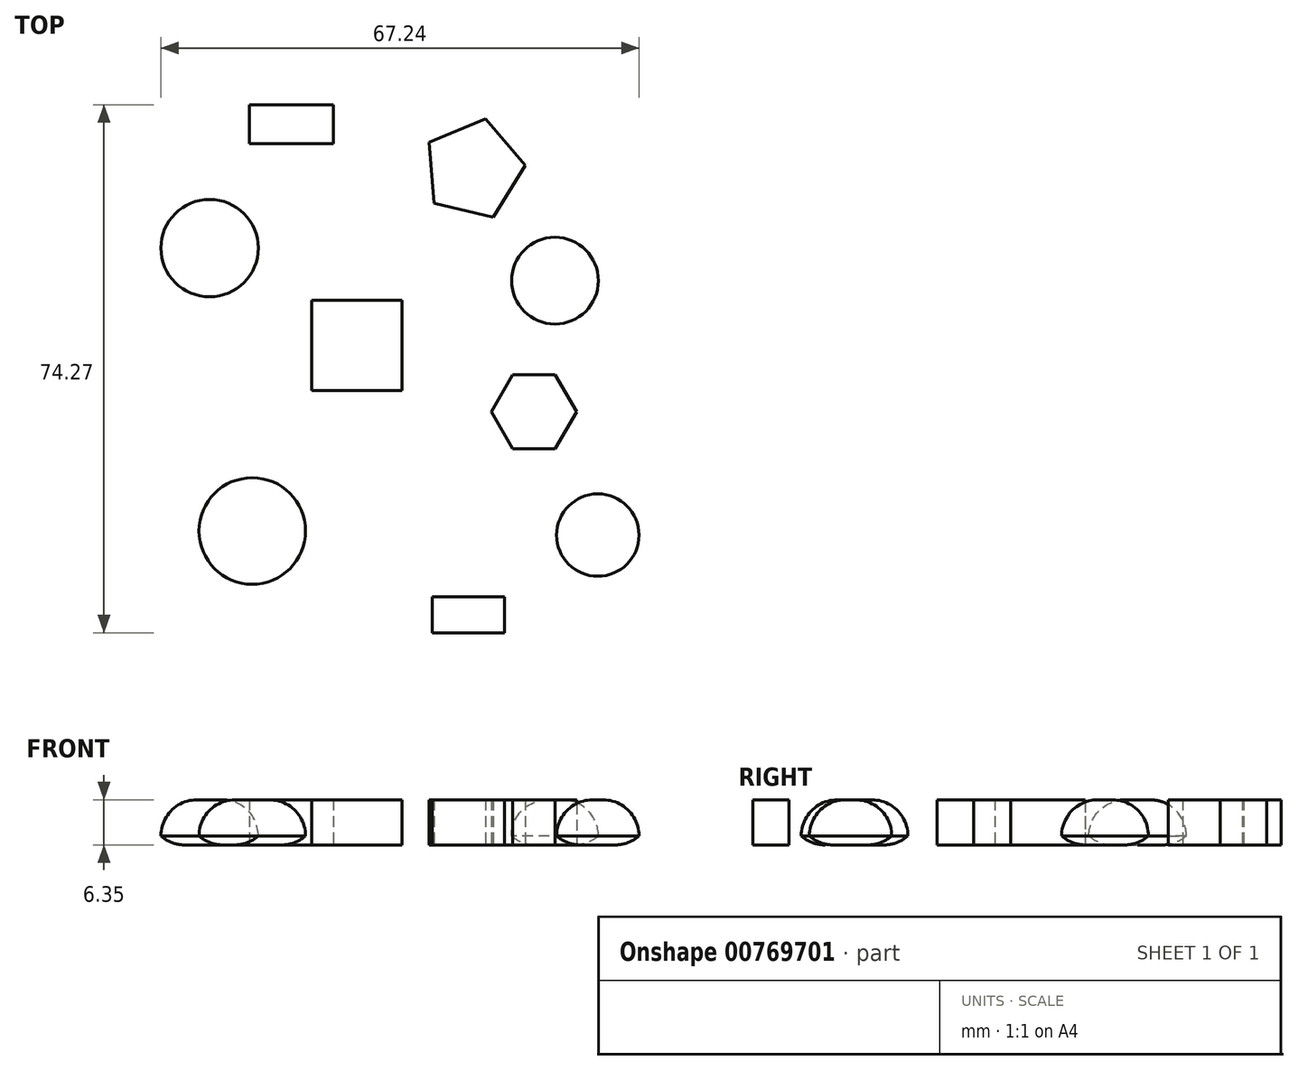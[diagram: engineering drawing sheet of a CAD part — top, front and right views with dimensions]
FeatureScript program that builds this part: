
annotation { "Feature Type Name" : "Feature", "Feature Type Description" : "" }
export const myFeature = defineFeature(function(context is Context, id is Id, definition is map)
    precondition{}
    {
        {
            var Q0;
            Q0=qCreatedBy(makeId("Top.planeOp"),FACE);
            var sketch = newSketch(context, id + "F0", { "sketchPlane" : qUnion([Q0])});
            skCircle(sketch, "E0", {"center": v(25.51, -24.88) * mm, "radius": 5.8 * mm});
            skSolve(sketch);
        }
        {
            var Q0;
            Q0=qCreatedBy(makeId("Top.planeOp"),FACE);
            var sketch = newSketch(context, id + "F1", { "sketchPlane" : qUnion([Q0])});
            skCircle(sketch, "E1", {"center": v(19.49, 10.92) * mm, "radius": 6.1 * mm});
            skSolve(sketch);
        }
        {
            var Q0;
            Q0=qCreatedBy(makeId("Top.planeOp"),FACE);
            var sketch = newSketch(context, id + "F2", { "sketchPlane" : qUnion([Q0])});
            skCircle(sketch, "E2", {"center": v(-29.08, 15.5) * mm, "radius": 6.85 * mm});
            skSolve(sketch);
        }
        {
            var Q0;
            Q0=qCreatedBy(makeId("Top.planeOp"),FACE);
            var sketch = newSketch(context, id + "F3", { "sketchPlane" : qUnion([Q0])});
            skCircle(sketch, "E3", {"center": v(-23.08, -24.3) * mm, "radius": 7.5 * mm});
            skSolve(sketch);
        }
        {
            var Q0;
            Q0=makeQuery(id+"F2.imprint","IMPRINT",FACE,{"disambiguationData":[TD([[makeQuery(id+"F2.imprint","IMPRINT",EDGE,{"derivedFrom":sQuery(id+"F2.wireOp",EDGE,"E2")}),1.0]])]});
            var Q1;
            Q1=makeQuery(id+"F1.imprint","IMPRINT",FACE,{"disambiguationData":[TD([[makeQuery(id+"F1.imprint","IMPRINT",EDGE,{"derivedFrom":sQuery(id+"F1.wireOp",EDGE,"E1")}),1.0]])]});
            var Q2;
            Q2=makeQuery(id+"F3.imprint","IMPRINT",FACE,{"disambiguationData":[TD([[makeQuery(id+"F3.imprint","IMPRINT",EDGE,{"derivedFrom":sQuery(id+"F3.wireOp",EDGE,"E3")}),1.0]])]});
            var Q3;
            Q3=makeQuery(id+"F0.imprint","IMPRINT",FACE,{"disambiguationData":[TD([[makeQuery(id+"F0.imprint","IMPRINT",EDGE,{"derivedFrom":sQuery(id+"F0.wireOp",EDGE,"E0")}),1.0]])]});
            extrude(context, id + "F4", {"entities" : qUnion([Q0, Q1, Q2, Q3]), "depth" : 6.35 * mm, "offsetDistance" : 25.4 * mm});
        }
        {
            var Q0;
            Q0=makeQuery(id+"F4.opExtrude","CAP_EDGE",EDGE,{"disambiguationData":[OSD([sQuery(id+"F2.wireOp",EDGE,"E2")])],"isStart":false});
            var Q1;
            Q1=makeQuery(id+"F4.opExtrude","CAP_EDGE",EDGE,{"disambiguationData":[OSD([sQuery(id+"F3.wireOp",EDGE,"E3")])],"isStart":false});
            var Q2;
            Q2=makeQuery(id+"F4.opExtrude","CAP_EDGE",EDGE,{"disambiguationData":[OSD([sQuery(id+"F1.wireOp",EDGE,"E1")])],"isStart":false});
            var Q3;
            Q3=makeQuery(id+"F4.opExtrude","CAP_EDGE",EDGE,{"disambiguationData":[OSD([sQuery(id+"F0.wireOp",EDGE,"E0")])],"isStart":false});
            fillet(context, id + "F5", {"entities" : qUnion([Q0, Q1, Q2, Q3]), "radius" : 5.08 * mm, "tangentPropagation" : true, "allowEdgeOverflow" : false});
        }
        {
            var Q0;
            Q0=makeQuery(id+"F4.opExtrude","CAP_EDGE",EDGE,{"disambiguationData":[OSD([sQuery(id+"F1.wireOp",EDGE,"E1")])],"isStart":true});
            var Q1;
            Q1=makeQuery(id+"F4.opExtrude","CAP_EDGE",EDGE,{"disambiguationData":[OSD([sQuery(id+"F2.wireOp",EDGE,"E2")])],"isStart":true});
            var Q2;
            Q2=makeQuery(id+"F4.opExtrude","CAP_EDGE",EDGE,{"disambiguationData":[OSD([sQuery(id+"F3.wireOp",EDGE,"E3")])],"isStart":true});
            var Q3;
            Q3=makeQuery(id+"F4.opExtrude","CAP_EDGE",EDGE,{"disambiguationData":[OSD([sQuery(id+"F0.wireOp",EDGE,"E0")])],"isStart":true});
            fillet(context, id + "F6", {"entities" : qUnion([Q0, Q1, Q2, Q3]), "radius" : 5.08 * mm, "tangentPropagation" : true, "allowEdgeOverflow" : false});
        }
        {
            var Q0;
            Q0=qCreatedBy(makeId("Top.planeOp"),FACE);
            var sketch = newSketch(context, id + "F7", { "sketchPlane" : qUnion([Q0])});
            skLineSegment(sketch, "E4.bottom", {"start": v(-14.74, 8.13) * mm, "end": v(-2.04, 8.13) * mm});
            skLineSegment(sketch, "E4.top", {"start": v(-14.74, -4.57) * mm, "end": v(-2.04, -4.57) * mm});
            skLineSegment(sketch, "E4.left", {"start": v(-14.74, 8.13) * mm, "end": v(-14.74, -4.57) * mm});
            skLineSegment(sketch, "E4.right", {"start": v(-2.04, 8.13) * mm, "end": v(-2.04, -4.57) * mm});
            skSolve(sketch);
        }
        {
            var Q0;
            Q0=qCreatedBy(makeId("Top.planeOp"),FACE);
            var sketch = newSketch(context, id + "F8", { "sketchPlane" : qUnion([Q0])});
            skLineSegment(sketch, "E5.bottom", {"start": v(2.27, -33.54) * mm, "end": v(12.43, -33.54) * mm});
            skLineSegment(sketch, "E5.top", {"start": v(2.27, -38.62) * mm, "end": v(12.43, -38.62) * mm});
            skLineSegment(sketch, "E5.left", {"start": v(2.27, -33.54) * mm, "end": v(2.27, -38.62) * mm});
            skLineSegment(sketch, "E5.right", {"start": v(12.43, -33.54) * mm, "end": v(12.43, -38.62) * mm});
            skSolve(sketch);
        }
        {
            var Q0;
            Q0=qCreatedBy(makeId("Top.planeOp"),FACE);
            var sketch = newSketch(context, id + "F9", { "sketchPlane" : qUnion([Q0])});
            skCircle(sketch, "E6.cCircle", {"center": v(16.53, -7.53) * mm, "radius": 5.2 * mm, "construction": true});
            skLineSegment(sketch, "E6.0", {"start": v(19.53, -12.72) * mm, "end": v(13.53, -12.72) * mm});
            skLineSegment(sketch, "E6.1", {"start": v(13.53, -12.72) * mm, "end": v(10.53, -7.53) * mm});
            skLineSegment(sketch, "E6.2", {"start": v(10.53, -7.53) * mm, "end": v(13.53, -2.34) * mm});
            skLineSegment(sketch, "E6.3", {"start": v(13.53, -2.34) * mm, "end": v(19.53, -2.34) * mm});
            skLineSegment(sketch, "E6.4", {"start": v(19.53, -2.34) * mm, "end": v(22.52, -7.53) * mm});
            skLineSegment(sketch, "E6.5", {"start": v(22.52, -7.53) * mm, "end": v(19.53, -12.72) * mm});
            skPoint(sketch, "E6.0.midPoint", {"position": v(16.53, -12.72) * mm});
            skSolve(sketch);
        }
        {
            var Q0;
            Q0=qCreatedBy(makeId("Top.planeOp"),FACE);
            var sketch = newSketch(context, id + "F10", { "sketchPlane" : qUnion([Q0])});
            skCircle(sketch, "E7.cCircle", {"center": v(8.03, 26.57) * mm, "radius": 5.91 * mm, "construction": true});
            skLineSegment(sketch, "E7.0", {"start": v(9.75, 33.67) * mm, "end": v(15.32, 27.13) * mm});
            skLineSegment(sketch, "E7.1", {"start": v(15.32, 27.13) * mm, "end": v(10.81, 19.81) * mm});
            skLineSegment(sketch, "E7.2", {"start": v(10.81, 19.81) * mm, "end": v(2.46, 21.84) * mm});
            skLineSegment(sketch, "E7.3", {"start": v(2.46, 21.84) * mm, "end": v(1.8, 30.4) * mm});
            skLineSegment(sketch, "E7.4", {"start": v(1.8, 30.4) * mm, "end": v(9.75, 33.67) * mm});
            skPoint(sketch, "E7.0.midPoint", {"position": v(12.53, 30.4) * mm});
            skSolve(sketch);
        }
        {
            var Q0;
            Q0=qCreatedBy(makeId("Top.planeOp"),FACE);
            var sketch = newSketch(context, id + "F11", { "sketchPlane" : qUnion([Q0])});
            skLineSegment(sketch, "E8.bottom", {"start": v(-23.48, 35.65) * mm, "end": v(-11.67, 35.65) * mm});
            skLineSegment(sketch, "E8.top", {"start": v(-23.48, 30.2) * mm, "end": v(-11.67, 30.2) * mm});
            skLineSegment(sketch, "E8.left", {"start": v(-23.48, 35.65) * mm, "end": v(-23.48, 30.2) * mm});
            skLineSegment(sketch, "E8.right", {"start": v(-11.67, 35.65) * mm, "end": v(-11.67, 30.2) * mm});
            skSolve(sketch);
        }
        {
            var Q0;
            Q0=makeQuery(id+"F11.imprint","IMPRINT",FACE,{"disambiguationData":[TD([[makeQuery(id+"F11.imprint","IMPRINT",EDGE,{"derivedFrom":sQuery(id+"F11.wireOp",EDGE,"E8.bottom")}),-1.0]])]});
            var Q1;
            Q1=makeQuery(id+"F10.imprint","IMPRINT",FACE,{"disambiguationData":[TD([[makeQuery(id+"F10.imprint","IMPRINT",EDGE,{"derivedFrom":sQuery(id+"F10.wireOp",EDGE,"E7.0")}),-1.0]])]});
            var Q2;
            Q2=makeQuery(id+"F7.imprint","IMPRINT",FACE,{"disambiguationData":[TD([[makeQuery(id+"F7.imprint","IMPRINT",EDGE,{"derivedFrom":sQuery(id+"F7.wireOp",EDGE,"E4.bottom")}),-1.0]])]});
            var Q3;
            Q3=makeQuery(id+"F9.imprint","IMPRINT",FACE,{"disambiguationData":[TD([[makeQuery(id+"F9.imprint","IMPRINT",EDGE,{"derivedFrom":sQuery(id+"F9.wireOp",EDGE,"E6.0")}),-1.0]])]});
            var Q4;
            Q4=makeQuery(id+"F8.imprint","IMPRINT",FACE,{"disambiguationData":[TD([[makeQuery(id+"F8.imprint","IMPRINT",EDGE,{"derivedFrom":sQuery(id+"F8.wireOp",EDGE,"E5.bottom")}),-1.0]])]});
            extrude(context, id + "F12", {"entities" : qUnion([Q0, Q1, Q2, Q3, Q4]), "depth" : 6.35 * mm, "offsetDistance" : 25.4 * mm});
        }
    });
